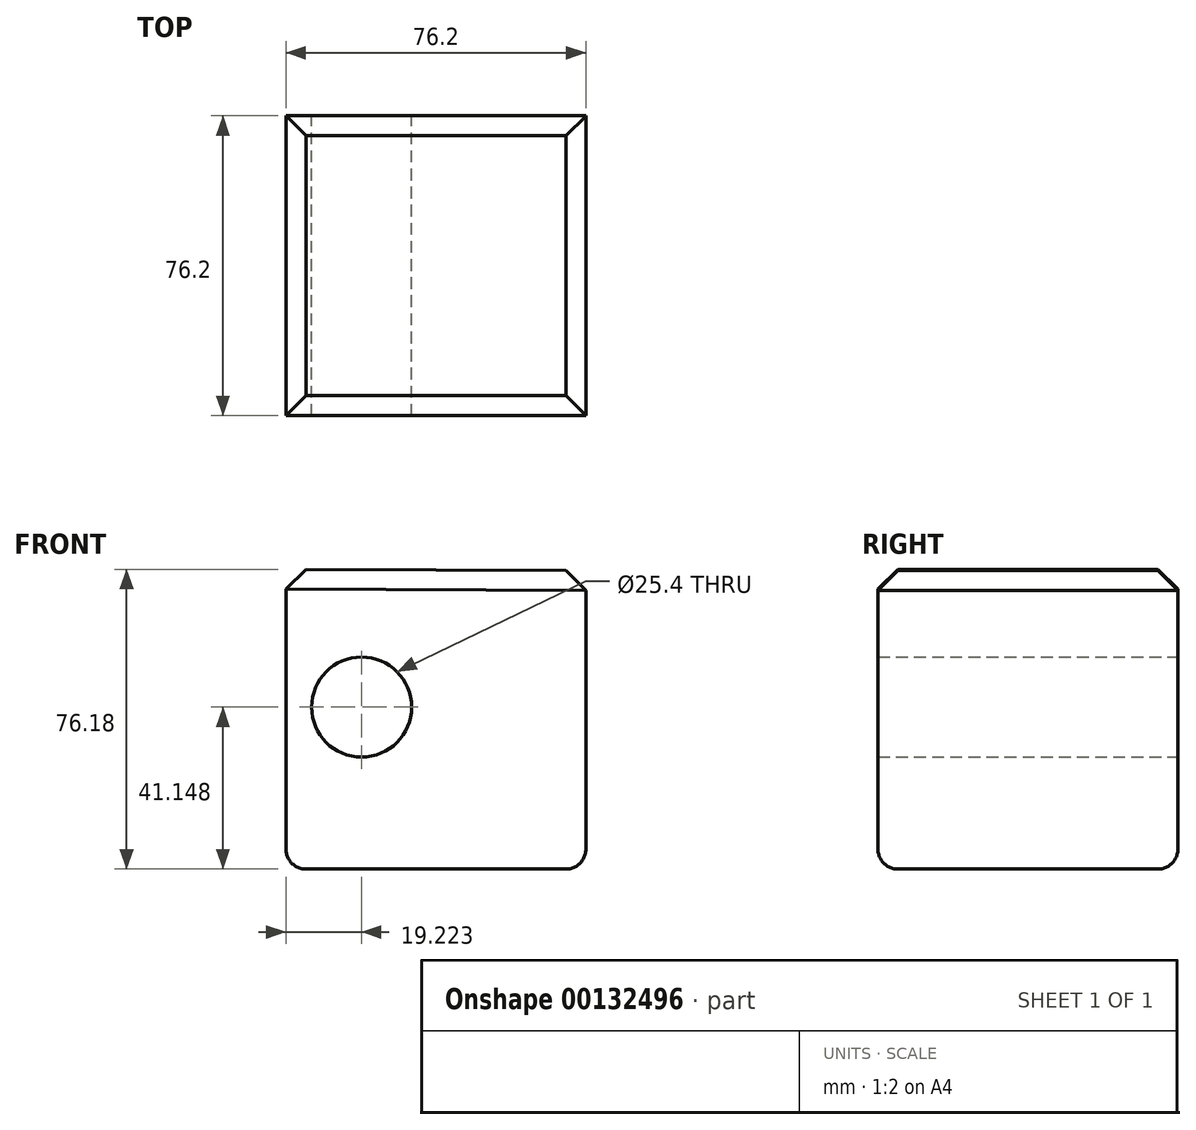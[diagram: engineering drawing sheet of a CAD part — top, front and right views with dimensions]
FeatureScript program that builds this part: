
annotation { "Feature Type Name" : "Feature", "Feature Type Description" : "" }
export const myFeature = defineFeature(function(context is Context, id is Id, definition is map)
    precondition{}
    {
        {
            var Q0;
            Q0=qCreatedBy(makeId("Front.planeOp"),FACE);
            var sketch = newSketch(context, id + "F0", { "sketchPlane" : qUnion([Q0])});
            skLineSegment(sketch, "E0", {"start": v(0, 76.2) * mm, "end": v(0, 0) * mm});
            skLineSegment(sketch, "E1", {"start": v(0, 0) * mm, "end": v(76.2, 0) * mm});
            skLineSegment(sketch, "E2", {"start": v(76.2, 0) * mm, "end": v(76.2, 75.85) * mm});
            skLineSegment(sketch, "E3", {"start": v(76.2, 75.85) * mm, "end": v(0, 76.2) * mm});
            skSolve(sketch);
        }
        {
            var Q0;
            Q0 = qSketchRegion(id + "F0", true);
            extrude(context, id + "F1", {"entities" : qUnion([Q0]), "depth" : 76.2 * mm});
        }
        {
            var Q0;
            Q0=makeQuery(id+"F1.opExtrude","SWEPT_FACE",FACE,{"disambiguationData":[OSD([sQuery(id+"F0.wireOp",EDGE,"E3")])]});
            chamfer(context, id + "F2", {"entities" : qUnion([Q0]), "width" : 5.08 * mm, "tangentPropagation" : true});
        }
        {
            var Q0;
            Q0=makeQuery(id+"F1.opExtrude","SWEPT_FACE",FACE,{"disambiguationData":[OSD([sQuery(id+"F0.wireOp",EDGE,"E1")])]});
            fillet(context, id + "F3", {"entities" : qUnion([Q0]), "radius" : 5.08 * mm, "tangentPropagation" : true, "allowEdgeOverflow" : false});
        }
        {
            var Q0;
            Q0=qCreatedBy(makeId("Front.planeOp"),FACE);
            var sketch = newSketch(context, id + "F4", { "sketchPlane" : qUnion([Q0])});
            skLineSegment(sketch, "E4", {"start": v(19.22, 41.15) * mm, "end": v(54.97, 41.15) * mm});
            skSolve(sketch);
        }
        {
            var Q0;
            Q0=sQuery(id+"F4.wireOp",VERTEX,"E4.start");
            var Q1;
            Q1=makeQuery(id+"F1.opExtrude","SWEPT_BODY",BODY,{"disambiguationData":[OSD([sQuery(id+"F0.wireOp",EDGE,"E0"),sQuery(id+"F0.wireOp",EDGE,"E1"),sQuery(id+"F0.wireOp",EDGE,"E2"),sQuery(id+"F0.wireOp",EDGE,"E3")])]});
            hole(context, id + "F5", {"style" : HoleStyle.SIMPLE, "endStyle" : HoleEndStyle.THROUGH, "oppositeDirection" : true, "holeDiameter" : 25.4 * mm, "locations" : qUnion([Q0]), "scope" : qUnion([Q1]), "isTappedThrough" : true});
        }
    });
